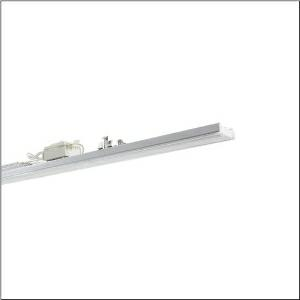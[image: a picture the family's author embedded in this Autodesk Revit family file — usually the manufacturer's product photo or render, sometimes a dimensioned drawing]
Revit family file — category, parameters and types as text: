
# Revit family: licross_r__21_recessed_mo_52tl18vn555g_0100
name_source: partatom
category: Lighting Fixtures
units: mm (PartAtom-declared; Revit-internal decimal feet)

## family parameters
Cut with Voids When Loaded = No
Host = Face
Light Source = No
Part Type = Normal
Room Calculation Point = No
Round Connector Dimension = Use Diameter
Shared = No

## types (1)
- --- (1 x LED, 5500 lm, 30.9 W, 5000K)
    Apparent Load = 31 VA
    CIE Flux Codes = 79 95 99 100 100
    Color Rendering = 80
    Color Temperature = 5000K
    Default Elevation = 1800 mm
    Description = Licross® 21 Recessed MO, luminaire insert, of sheet steel, galvanised, coil coated, white, length: 1.500mm, width: 66mm, height: 67mm, LED rated luminous flux: 5.500lm, light colour: 850, control gear: DALI 2, CLO, with plug, 5-pole, with phase selection, mains connection: 220..240V, AC, 50/60Hz, start of lifetime: 31W, end of service life: 37W, halogen-free wiring, primary optical cover: cover, of PMMA, light emission: direct distribution, primary light characteristic: symmetric, protection rating (complete): IP40, insulation class (complete): insulation class I (protective earthing), certification: CE, ENEC, VDE, UKCA, protection symbol: D if used in an environment without relevant dust loads with corresponding accessories, impact resistance: IK06, permissible ambient temperature for indoor applications: -25..+45°C, corresponds to IFS (International Featured Standards) requirements for safety and quality in the food industry, reducing of maximum allowable ambient temperature of 5°C with ceiling mounting, LABS conformity tested according to VDMA 24364:2018-05, packaging unit: 1 piece
    Height = 58 mm
    Lamp = 1 x LED
    Lamp Light Flux = 5500 lm
    Lamp Power = 30.9 W
    Lamp count = 1
    Length = 1500 mm
    Luminous efficacy = 178 lm/W
    Manufacturer = Siteco
    ModVariant = No
    Model = 52TL18VN555G
    Mounting Place = Ceiling
    Mounting Type = Pendant
    Number of Poles = 1
    OnlyDefault = Yes
    Power Factor = 1
    Product Name = Licross® 21 Recessed MO
    Product group = luminaire insert
    ProductGroupID = 902
    Protection Class = Protection class I
    Protection Degree = IP 40
    RLX_Detail_Level = 1
    RLX_Emergency_Light_Flux = 0 lm
    RLX_Emergency_Type = 0
    RLX_Emergency_Type_DB = No
    RlxData = <blob elided: 23961 chars, md5=e8a409d9>
    Socket = socket
    Standby Power = 0 W
    System Light Flux = 5500 lm
    System Power = 31 W
    Type Comments = factory setting: luminous flux: 100 % | dim-lin: 254 | 209 mA
    Type Image = l_1296930.jpg
    URL = http://relux.com
    VarID = @adj_082080
    Voltage = 0 V
    Weight = 0.00 kg
    Width = 66 mm

## geometry (parser evidence)
native form markers: Blend x4, Sweep x10
no freeform markers — native parametric forms only
